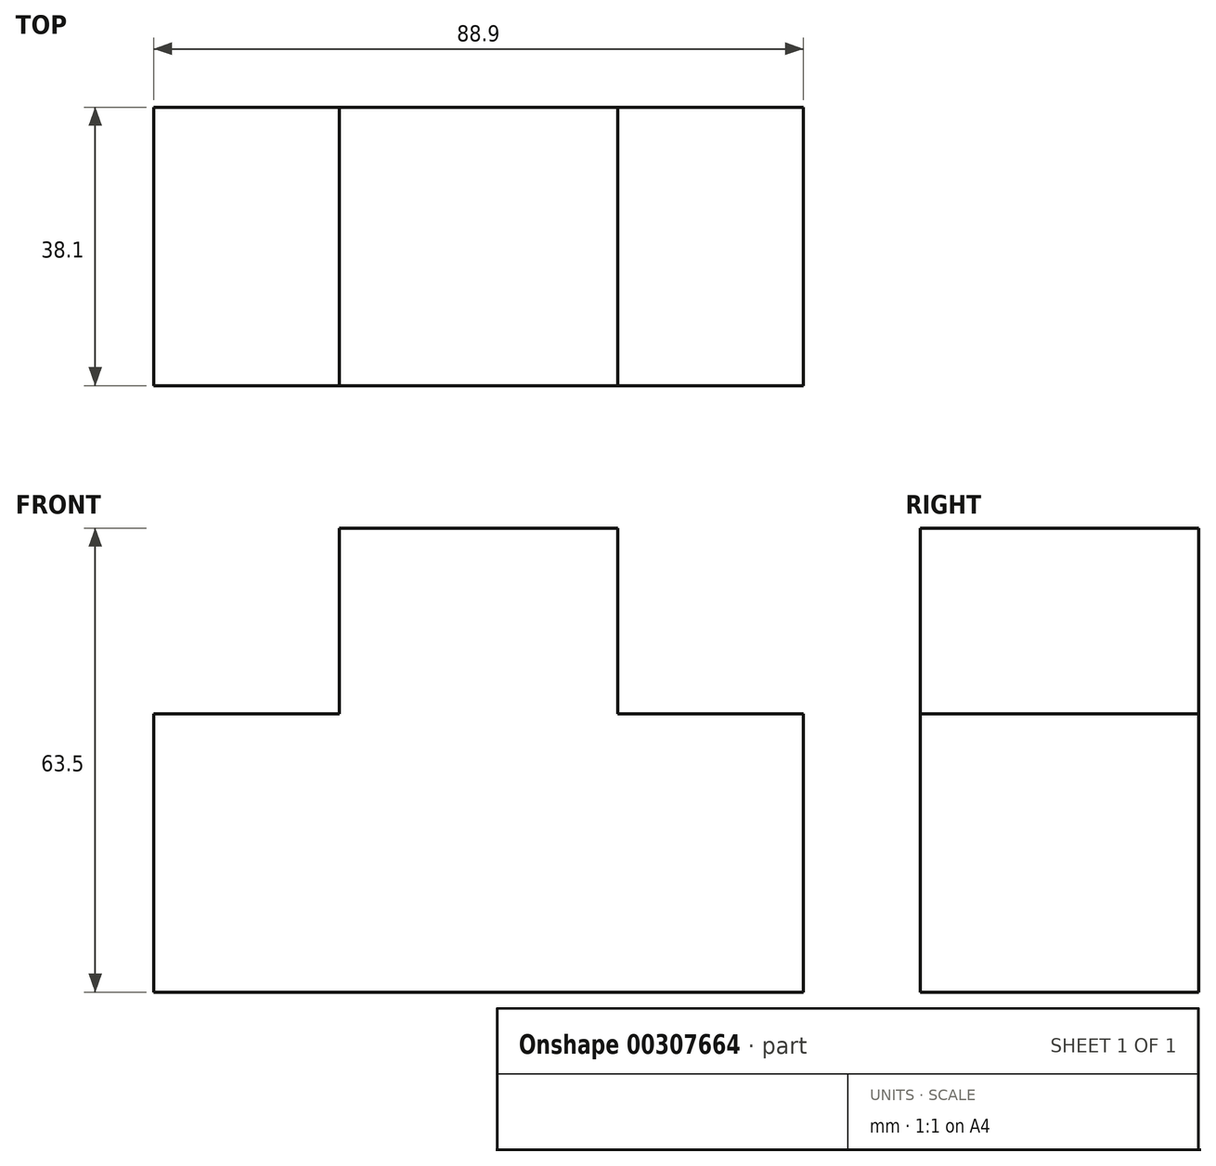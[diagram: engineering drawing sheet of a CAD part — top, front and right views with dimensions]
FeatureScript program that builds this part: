
annotation { "Feature Type Name" : "Feature", "Feature Type Description" : "" }
export const myFeature = defineFeature(function(context is Context, id is Id, definition is map)
    precondition{}
    {
        {
            var Q0;
            Q0=qCreatedBy(makeId("Front.planeOp"),FACE);
            var sketch = newSketch(context, id + "F0", { "sketchPlane" : qUnion([Q0])});
            skLineSegment(sketch, "E0", {"start": v(-31.3, -37.06) * mm, "end": v(57.6, -37.06) * mm});
            skLineSegment(sketch, "E1", {"start": v(57.6, -37.06) * mm, "end": v(57.6, 1.04) * mm});
            skLineSegment(sketch, "E2", {"start": v(57.6, 1.04) * mm, "end": v(32.2, 1.04) * mm});
            skLineSegment(sketch, "E3", {"start": v(32.2, 1.04) * mm, "end": v(32.2, 26.44) * mm});
            skLineSegment(sketch, "E4", {"start": v(32.2, 26.44) * mm, "end": v(-5.9, 26.44) * mm});
            skLineSegment(sketch, "E5", {"start": v(-5.9, 26.44) * mm, "end": v(-5.9, 1.04) * mm});
            skLineSegment(sketch, "E6", {"start": v(-5.9, 1.04) * mm, "end": v(-31.3, 1.04) * mm});
            skLineSegment(sketch, "E7", {"start": v(-31.3, 1.04) * mm, "end": v(-31.3, -37.06) * mm});
            skSolve(sketch);
        }
        {
            var Q0;
            Q0=makeQuery(id+"F0.imprint","IMPRINT",FACE,{"disambiguationData":[TD([[makeQuery(id+"F0.imprint","IMPRINT",EDGE,{"derivedFrom":sQuery(id+"F0.wireOp",EDGE,"E0")}),1.0]])]});
            extrude(context, id + "F1", {"entities" : qUnion([Q0]), "depth" : 38.1 * mm});
        }
    });
